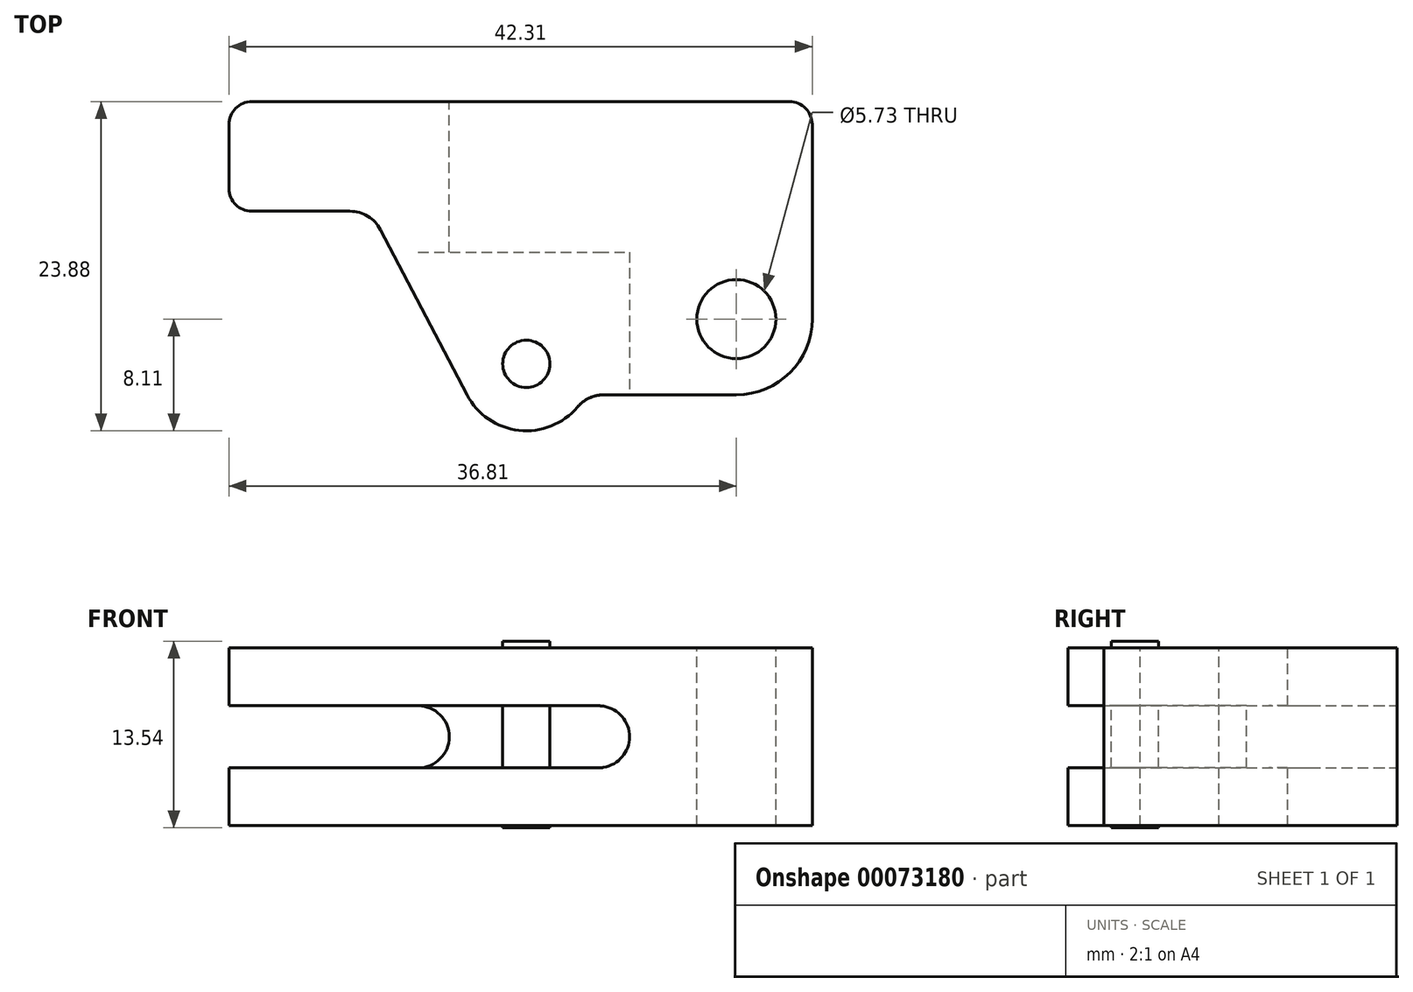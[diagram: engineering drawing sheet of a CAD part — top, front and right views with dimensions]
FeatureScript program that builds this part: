
annotation { "Feature Type Name" : "Feature", "Feature Type Description" : "" }
export const myFeature = defineFeature(function(context is Context, id is Id, definition is map)
    precondition{}
    {
        {
            var Q0;
            Q0=qCreatedBy(makeId("Top.planeOp"),FACE);
            var sketch = newSketch(context, id + "F0", { "sketchPlane" : qUnion([Q0])});
            skLineSegment(sketch, "E0", {"start": v(-21.57, 19.02) * mm, "end": v(20.74, 19.02) * mm});
            skLineSegment(sketch, "E1", {"start": v(20.74, 19.02) * mm, "end": v(20.74, -2.25) * mm});
            skLineSegment(sketch, "E2", {"start": v(20.74, -2.25) * mm, "end": v(-4.3, -2.25) * mm});
            skLineSegment(sketch, "E3", {"start": v(-4.3, -2.25) * mm, "end": v(-11.28, 11.07) * mm});
            skLineSegment(sketch, "E4", {"start": v(-11.28, 11.07) * mm, "end": v(-21.57, 11.07) * mm});
            skLineSegment(sketch, "E5", {"start": v(-21.57, 11.07) * mm, "end": v(-21.57, 19.02) * mm});
            skCircle(sketch, "E6", {"center": v(0, 0) * mm, "radius": 1.72 * mm});
            skCircle(sketch, "E7", {"center": v(0, 0) * mm, "radius": 4.86 * mm});
            skSolve(sketch);
        }
        {
            var Q0;
            Q0 = qSketchRegion(id + "F0", true);
            extrude(context, id + "F1", {"entities" : qUnion([Q0]), "depth" : 12.9 * mm});
        }
        {
            var Q0;
            Q0=makeQuery(id+"F1.opExtrude","SWEPT_EDGE",EDGE,{"disambiguationData":[OSD([sQuery(id+"F0.wireOp",EDGE,"E0"),sQuery(id+"F0.wireOp",EDGE,"E5")])]});
            var Q1;
            Q1=makeQuery(id+"F1.opExtrude","SWEPT_EDGE",EDGE,{"disambiguationData":[OSD([sQuery(id+"F0.wireOp",EDGE,"E4"),sQuery(id+"F0.wireOp",EDGE,"E5")])]});
            var Q2;
            Q2=makeQuery(id+"F1.opExtrude","SWEPT_EDGE",EDGE,{"disambiguationData":[OSD([sQuery(id+"F0.wireOp",EDGE,"E0"),sQuery(id+"F0.wireOp",EDGE,"E1")])]});
            fillet(context, id + "F2", {"entities" : qUnion([Q0, Q1, Q2]), "radius" : 1.65 * mm, "tangentPropagation" : true, "allowEdgeOverflow" : false});
        }
        {
            var Q0;
            Q0=makeQuery(id+"F1.opExtrude","SWEPT_EDGE",EDGE,{"disambiguationData":[OSD([sQuery(id+"F0.wireOp",EDGE,"E3"),sQuery(id+"F0.wireOp",EDGE,"E4")])]});
            var Q1;
            {var subQ0=sQuery(id+"F0.wireOp",EDGE,"E7");var subQ1=sQuery(id+"F0.wireOp",EDGE,"E2");Q1=makeQuery(id+"F1.opExtrude","SWEPT_EDGE",EDGE,{"disambiguationData":[OSD([subQ1,subQ0]),TDD([makeQuery(id+"F0.imprint","INTERSECT",VERTEX,{"disambiguationData":[OD(0.0)],"derivedFrom":[subQ1,subQ0]})])]});}
            fillet(context, id + "F3", {"entities" : qUnion([Q0, Q1]), "radius" : 2.5 * mm, "tangentPropagation" : true, "allowEdgeOverflow" : false});
        }
        {
            var Q0;
            Q0=makeQuery(id+"F1.opExtrude","SWEPT_EDGE",EDGE,{"disambiguationData":[OSD([sQuery(id+"F0.wireOp",EDGE,"E1"),sQuery(id+"F0.wireOp",EDGE,"E2")])]});
            fillet(context, id + "F4", {"entities" : qUnion([Q0]), "radius" : 5.5 * mm, "tangentPropagation" : true, "allowEdgeOverflow" : false});
        }
        {
            var Q0;
            Q0=makeQuery(id+"F1.opExtrude","CAP_FACE",FACE,{"disambiguationData":[OSD([sQuery(id+"F0.wireOp",EDGE,"E0"),sQuery(id+"F0.wireOp",EDGE,"E1"),sQuery(id+"F0.wireOp",EDGE,"E2"),sQuery(id+"F0.wireOp",EDGE,"E3"),sQuery(id+"F0.wireOp",EDGE,"E4"),sQuery(id+"F0.wireOp",EDGE,"E5"),sQuery(id+"F0.wireOp",EDGE,"E6"),sQuery(id+"F0.wireOp",EDGE,"E7")])],"isStart":false});
            var sketch = newSketch(context, id + "F5", { "sketchPlane" : qUnion([Q0])});
            skCircle(sketch, "E8", {"center": v(15.24, 3.25) * mm, "radius": 2.87 * mm});
            skSolve(sketch);
        }
        {
            var Q0;
            Q0 = qSketchRegion(id + "F5", true);
            extrude(context, id + "F6", {"entities" : qUnion([Q0]), "operationType" : NewBodyOperationType.REMOVE, "endBound" : BoundingType.THROUGH_ALL, "oppositeDirection" : true, "depth" : 25 * mm});
        }
        {
            var Q0;
            Q0=makeQuery(id+"F1.opExtrude","SWEPT_FACE",FACE,{"disambiguationData":[OSD([sQuery(id+"F0.wireOp",EDGE,"E0")])]});
            var sketch = newSketch(context, id + "F7", { "sketchPlane" : qUnion([Q0])});
            skLineSegment(sketch, "E9.bottom", {"start": v(7.84, 4.2) * mm, "end": v(22, 4.2) * mm});
            skLineSegment(sketch, "E9.top", {"start": v(7.84, 8.7) * mm, "end": v(22, 8.7) * mm});
            skLineSegment(sketch, "E9.left", {"start": v(7.84, 4.2) * mm, "end": v(7.84, 8.7) * mm});
            skLineSegment(sketch, "E9.right", {"start": v(22, 4.2) * mm, "end": v(22, 8.7) * mm});
            skCircle(sketch, "E10", {"center": v(7.84, 6.44) * mm, "radius": 2.25 * mm});
            skSolve(sketch);
        }
        {
            var Q0;
            Q0 = qSketchRegion(id + "F7", true);
            extrude(context, id + "F8", {"entities" : qUnion([Q0]), "operationType" : NewBodyOperationType.REMOVE, "endBound" : BoundingType.UP_TO_NEXT, "oppositeDirection" : true, "depth" : 25 * mm});
        }
        {
            var Q0;
            Q0=makeQuery(id+"F1.opExtrude","SWEPT_FACE",FACE,{"disambiguationData":[OSD([sQuery(id+"F0.wireOp",EDGE,"E2")])]});
            var sketch = newSketch(context, id + "F9", { "sketchPlane" : qUnion([Q0])});
            skLineSegment(sketch, "E11.bottom", {"start": v(-9.1, 8.7) * mm, "end": v(5.24, 8.7) * mm});
            skLineSegment(sketch, "E11.top", {"start": v(-9.1, 4.2) * mm, "end": v(5.24, 4.2) * mm});
            skLineSegment(sketch, "E11.left", {"start": v(-9.1, 8.7) * mm, "end": v(-9.1, 4.2) * mm});
            skLineSegment(sketch, "E11.right", {"start": v(5.24, 8.7) * mm, "end": v(5.24, 4.2) * mm});
            skCircle(sketch, "E12", {"center": v(5.24, 6.45) * mm, "radius": 2.25 * mm});
            skSolve(sketch);
        }
        {
            var Q0;
            Q0 = qSketchRegion(id + "F9", true);
            extrude(context, id + "F10", {"entities" : qUnion([Q0]), "operationType" : NewBodyOperationType.REMOVE, "oppositeDirection" : true, "depth" : 10.35 * mm, "hasSecondDirection" : true, "secondDirectionBound" : SecondDirectionBoundingType.THROUGH_ALL, "secondDirectionOppositeDirection" : false, "secondDirectionDepth" : 5.39 * mm});
        }
        {
            var Q0;
            Q0=makeQuery(id+"F1.opExtrude","CAP_FACE",FACE,{"disambiguationData":[OSD([sQuery(id+"F0.wireOp",EDGE,"E0"),sQuery(id+"F0.wireOp",EDGE,"E1"),sQuery(id+"F0.wireOp",EDGE,"E2"),sQuery(id+"F0.wireOp",EDGE,"E3"),sQuery(id+"F0.wireOp",EDGE,"E4"),sQuery(id+"F0.wireOp",EDGE,"E5"),sQuery(id+"F0.wireOp",EDGE,"E6"),sQuery(id+"F0.wireOp",EDGE,"E7")])],"isStart":false});
            var sketch = newSketch(context, id + "F11", { "sketchPlane" : qUnion([Q0])});
            skCircle(sketch, "E13", {"center": v(0, 0) * mm, "radius": 1.71 * mm});
            skSolve(sketch);
        }
        {
            var Q0;
            Q0 = qSketchRegion(id + "F11", true);
            extrude(context, id + "F12", {"entities" : qUnion([Q0]), "operationType" : NewBodyOperationType.ADD, "oppositeDirection" : true, "depth" : 13.04 * mm, "hasSecondDirection" : true, "secondDirectionOppositeDirection" : false, "secondDirectionDepth" : 0.5 * mm});
        }
    });
